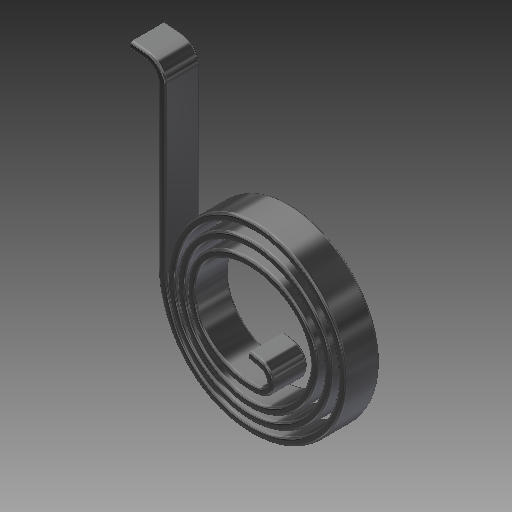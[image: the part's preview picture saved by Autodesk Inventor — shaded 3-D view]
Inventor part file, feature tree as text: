
AUTODESK INVENTOR PART (.ipt)
format: ipt  version: 2019 (Build 230136000, 136)  size: 732,160 bytes
history: native  units: mm
features: extrude x1, fillet x1, sketch x1
ambient origin geometry x8: Origin, YZ Plane, XZ Plane, XY Plane, X Axis, Y Axis, Z Axis, Center Point
bodies: Solid1 (feature_tree)
feature tree (3):
  extrude  "Extrusion1"  Depth=1.0mm
  fillet  "Fillet1"  [1 undecoded]
  sketch  "Sketch1"  dims[d0=12.5mm d1=0.0mm d2=1.0mm]
note: 1 required parameter value undecoded (feature->parameter linkage not recoverable at this tier; creation-order binding heuristic only, values carry confidence <= 0.55)
